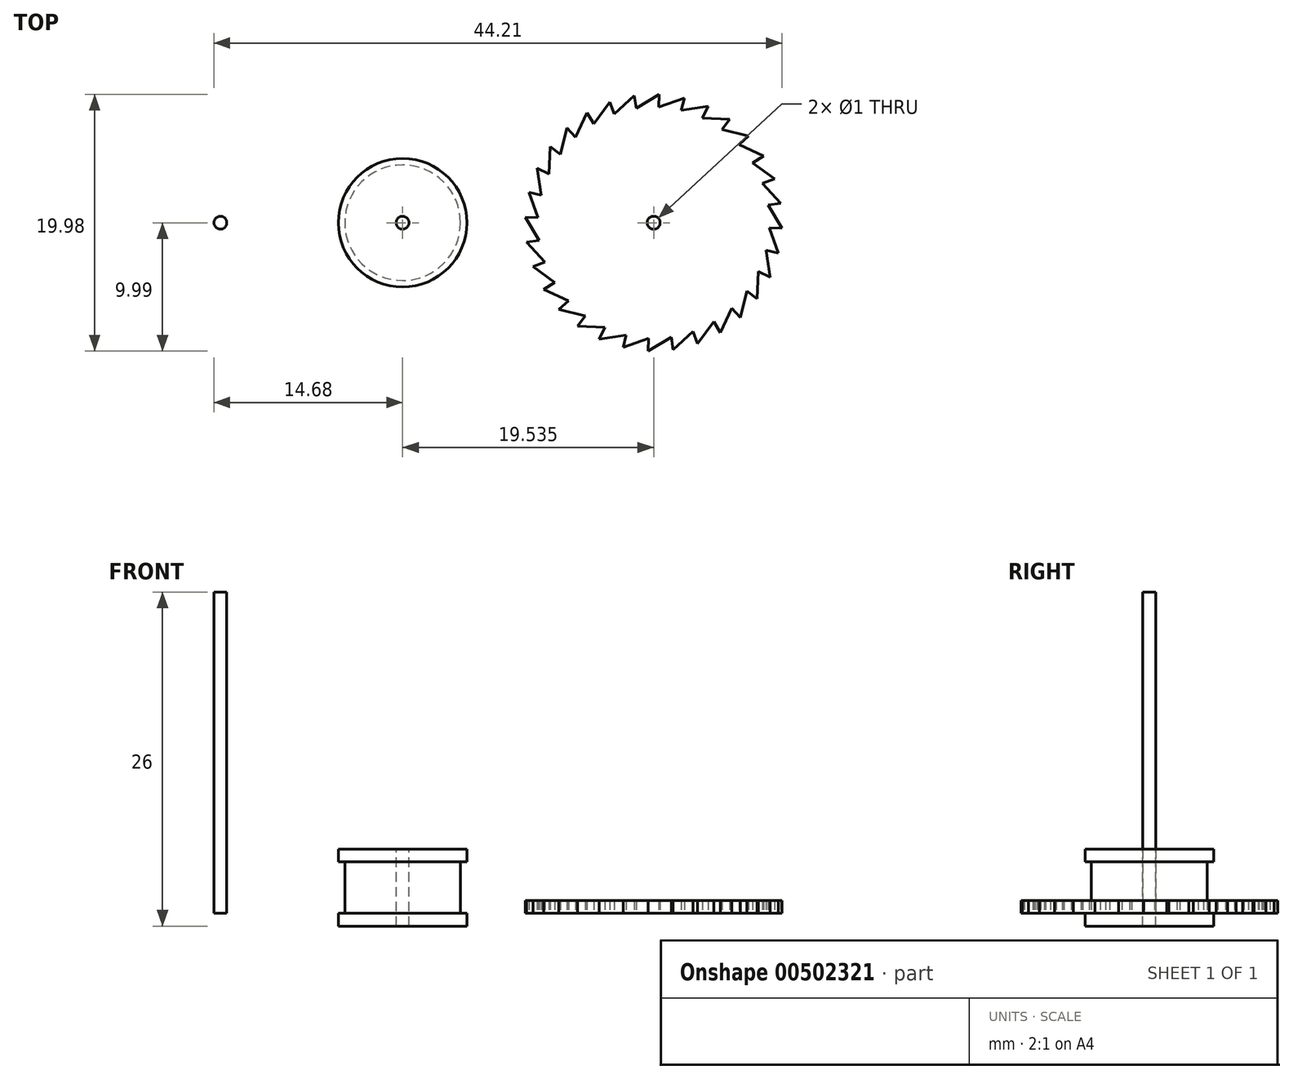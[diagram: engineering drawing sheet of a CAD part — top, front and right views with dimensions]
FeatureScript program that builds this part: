
annotation { "Feature Type Name" : "Feature", "Feature Type Description" : "" }
export const myFeature = defineFeature(function(context is Context, id is Id, definition is map)
    precondition{}
    {
        {
            var Q0;
            Q0=qCreatedBy(makeId("Top.planeOp"),FACE);
            var sketch = newSketch(context, id + "F0", { "sketchPlane" : qUnion([Q0])});
            skCircle(sketch, "E0", {"center": v(0, 0) * mm, "radius": 5 * mm});
            skCircle(sketch, "E1", {"center": v(0, 0) * mm, "radius": 4.5 * mm});
            skCircle(sketch, "E2", {"center": v(0, 0) * mm, "radius": 0.5 * mm});
            skSolve(sketch);
        }
        {
            var Q0;
            Q0=makeQuery(id+"F0.imprint","IMPRINT",FACE,{"disambiguationData":[TD([[makeQuery(id+"F0.imprint","IMPRINT",EDGE,{"derivedFrom":sQuery(id+"F0.wireOp",EDGE,"E0")}),1.0]])]});
            var Q1;
            Q1=makeQuery(id+"F0.imprint","IMPRINT",FACE,{"disambiguationData":[TD([[makeQuery(id+"F0.imprint","IMPRINT",EDGE,{"derivedFrom":sQuery(id+"F0.wireOp",EDGE,"E1")}),1.0]])]});
            extrude(context, id + "F1", {"entities" : qUnion([Q0, Q1]), "oppositeDirection" : true, "depth" : 1 * mm, "offsetDistance" : 25 * mm});
        }
        {
            var Q0;
            Q0=makeQuery(id+"F0.imprint","IMPRINT",FACE,{"disambiguationData":[TD([[makeQuery(id+"F0.imprint","IMPRINT",EDGE,{"derivedFrom":sQuery(id+"F0.wireOp",EDGE,"E1")}),1.0]])]});
            extrude(context, id + "F2", {"entities" : qUnion([Q0]), "operationType" : NewBodyOperationType.ADD, "depth" : 2 * mm, "offsetDistance" : 25 * mm});
        }
        {
            var Q0;
            Q0=makeQuery(id+"F1.opExtrude","SWEPT_BODY",BODY,{"disambiguationData":[OSD([sQuery(id+"F0.wireOp",EDGE,"E0")])]});
            var Q1;
            Q1=makeQuery(id+"F2.opExtrude","CAP_FACE",FACE,{"disambiguationData":[OSD([sQuery(id+"F0.wireOp",EDGE,"E1")])],"isStart":false});
            mirror(context, id + "F3", {"operationType" : NewBodyOperationType.ADD, "entities" : qUnion([Q0]), "mirrorPlane" : qUnion([Q1])});
        }
        {
            var Q0;
            Q0=qCreatedBy(makeId("Top.planeOp"),FACE);
            var sketch = newSketch(context, id + "F4", { "sketchPlane" : qUnion([Q0])});
            skCircle(sketch, "E3", {"center": v(-14.18, 0) * mm, "radius": 0.5 * mm});
            skCircle(sketch, "E4", {"center": v(19.53, 0) * mm, "radius": 9 * mm, "construction": true});
            skCircle(sketch, "E5", {"center": v(19.53, 0) * mm, "radius": 0.5 * mm});
            skCircle(sketch, "E6", {"center": v(19.53, 0) * mm, "radius": 10 * mm, "construction": true});
            skLineSegment(sketch, "E7", {"start": v(19.53, 0) * mm, "end": v(21.91, 9.71) * mm, "construction": true});
            skLineSegment(sketch, "E8.1.0", {"start": v(19.53, 0) * mm, "end": v(19.97, 10) * mm, "construction": true});
            skLineSegment(sketch, "E8.2.0", {"start": v(19.53, 0) * mm, "end": v(18.02, 9.88) * mm, "construction": true});
            skLineSegment(sketch, "E8.3.0", {"start": v(19.53, 0) * mm, "end": v(16.12, 9.4) * mm, "construction": true});
            skLineSegment(sketch, "E8.4.0", {"start": v(19.53, 0) * mm, "end": v(14.35, 8.55) * mm, "construction": true});
            skLineSegment(sketch, "E8.5.0", {"start": v(19.53, 0) * mm, "end": v(12.78, 7.37) * mm, "construction": true});
            skLineSegment(sketch, "E8.6.0", {"start": v(19.53, 0) * mm, "end": v(11.47, 5.92) * mm, "construction": true});
            skLineSegment(sketch, "E8.7.0", {"start": v(19.53, 0) * mm, "end": v(10.47, 4.23) * mm, "construction": true});
            skLineSegment(sketch, "E8.8.0", {"start": v(19.53, 0) * mm, "end": v(9.82, 2.38) * mm, "construction": true});
            skLineSegment(sketch, "E8.9.0", {"start": v(19.53, 0) * mm, "end": v(9.54, 0.44) * mm, "construction": true});
            skLineSegment(sketch, "E8.10.0", {"start": v(19.53, 0) * mm, "end": v(9.65, -1.52) * mm, "construction": true});
            skLineSegment(sketch, "E8.11.0", {"start": v(19.53, 0) * mm, "end": v(10.14, -3.42) * mm, "construction": true});
            skLineSegment(sketch, "E8.12.0", {"start": v(19.53, 0) * mm, "end": v(10.98, -5.18) * mm, "construction": true});
            skLineSegment(sketch, "E8.13.0", {"start": v(19.53, 0) * mm, "end": v(12.16, -6.75) * mm, "construction": true});
            skLineSegment(sketch, "E8.14.0", {"start": v(19.53, 0) * mm, "end": v(13.62, -8.06) * mm, "construction": true});
            skLineSegment(sketch, "E8.15.0", {"start": v(19.53, 0) * mm, "end": v(15.3, -9.06) * mm, "construction": true});
            skLineSegment(sketch, "E8.16.0", {"start": v(19.53, 0) * mm, "end": v(17.15, -9.71) * mm, "construction": true});
            skLineSegment(sketch, "E8.17.0", {"start": v(19.53, 0) * mm, "end": v(19.1, -10) * mm, "construction": true});
            skLineSegment(sketch, "E8.18.0", {"start": v(19.53, 0) * mm, "end": v(21.05, -9.88) * mm, "construction": true});
            skLineSegment(sketch, "E8.19.0", {"start": v(19.53, 0) * mm, "end": v(22.95, -9.4) * mm, "construction": true});
            skLineSegment(sketch, "E8.20.0", {"start": v(19.53, 0) * mm, "end": v(24.72, -8.55) * mm, "construction": true});
            skLineSegment(sketch, "E8.21.0", {"start": v(19.53, 0) * mm, "end": v(26.29, -7.37) * mm, "construction": true});
            skLineSegment(sketch, "E8.22.0", {"start": v(19.53, 0) * mm, "end": v(27.6, -5.92) * mm, "construction": true});
            skLineSegment(sketch, "E8.23.0", {"start": v(19.53, 0) * mm, "end": v(28.6, -4.23) * mm, "construction": true});
            skLineSegment(sketch, "E8.24.0", {"start": v(19.53, 0) * mm, "end": v(29.25, -2.38) * mm, "construction": true});
            skLineSegment(sketch, "E8.25.0", {"start": v(19.53, 0) * mm, "end": v(29.53, -0.44) * mm, "construction": true});
            skLineSegment(sketch, "E8.26.0", {"start": v(19.53, 0) * mm, "end": v(29.42, 1.52) * mm, "construction": true});
            skLineSegment(sketch, "E8.27.0", {"start": v(19.53, 0) * mm, "end": v(28.93, 3.42) * mm, "construction": true});
            skLineSegment(sketch, "E8.28.0", {"start": v(19.53, 0) * mm, "end": v(28.09, 5.18) * mm, "construction": true});
            skLineSegment(sketch, "E8.29.0", {"start": v(19.53, 0) * mm, "end": v(26.9, 6.75) * mm, "construction": true});
            skLineSegment(sketch, "E8.30.0", {"start": v(19.53, 0) * mm, "end": v(25.45, 8.06) * mm, "construction": true});
            skLineSegment(sketch, "E8.31.0", {"start": v(19.53, 0) * mm, "end": v(23.76, 9.06) * mm, "construction": true});
            skLineSegment(sketch, "E9", {"start": v(21.68, 8.74) * mm, "end": v(21.91, 9.71) * mm});
            skLineSegment(sketch, "E10", {"start": v(21.91, 9.71) * mm, "end": v(19.93, 9) * mm});
            skLineSegment(sketch, "E11.1.0", {"start": v(19.97, 10) * mm, "end": v(18.17, 8.9) * mm});
            skLineSegment(sketch, "E11.1.1", {"start": v(19.93, 9) * mm, "end": v(19.97, 10) * mm});
            skLineSegment(sketch, "E11.2.0", {"start": v(18.02, 9.88) * mm, "end": v(16.46, 8.46) * mm});
            skLineSegment(sketch, "E11.2.1", {"start": v(18.17, 8.9) * mm, "end": v(18.02, 9.88) * mm});
            skLineSegment(sketch, "E11.3.0", {"start": v(16.12, 9.4) * mm, "end": v(14.87, 7.7) * mm});
            skLineSegment(sketch, "E11.3.1", {"start": v(16.46, 8.46) * mm, "end": v(16.12, 9.4) * mm});
            skLineSegment(sketch, "E11.4.0", {"start": v(14.35, 8.55) * mm, "end": v(13.46, 6.64) * mm});
            skLineSegment(sketch, "E11.4.1", {"start": v(14.87, 7.7) * mm, "end": v(14.35, 8.55) * mm});
            skLineSegment(sketch, "E11.5.0", {"start": v(12.78, 7.37) * mm, "end": v(12.28, 5.32) * mm});
            skLineSegment(sketch, "E11.5.1", {"start": v(13.46, 6.64) * mm, "end": v(12.78, 7.37) * mm});
            skLineSegment(sketch, "E11.6.0", {"start": v(11.47, 5.92) * mm, "end": v(11.38, 3.8) * mm});
            skLineSegment(sketch, "E11.6.1", {"start": v(12.28, 5.32) * mm, "end": v(11.47, 5.92) * mm});
            skLineSegment(sketch, "E11.7.0", {"start": v(10.47, 4.23) * mm, "end": v(10.8, 2.14) * mm});
            skLineSegment(sketch, "E11.7.1", {"start": v(11.38, 3.8) * mm, "end": v(10.47, 4.23) * mm});
            skLineSegment(sketch, "E11.8.0", {"start": v(9.82, 2.38) * mm, "end": v(10.54, 0.4) * mm});
            skLineSegment(sketch, "E11.8.1", {"start": v(10.8, 2.14) * mm, "end": v(9.82, 2.38) * mm});
            skLineSegment(sketch, "E11.9.0", {"start": v(9.54, 0.44) * mm, "end": v(10.64, -1.37) * mm});
            skLineSegment(sketch, "E11.9.1", {"start": v(10.54, 0.4) * mm, "end": v(9.54, 0.44) * mm});
            skLineSegment(sketch, "E11.10.0", {"start": v(9.65, -1.52) * mm, "end": v(11.08, -3.08) * mm});
            skLineSegment(sketch, "E11.10.1", {"start": v(10.64, -1.37) * mm, "end": v(9.65, -1.52) * mm});
            skLineSegment(sketch, "E11.11.0", {"start": v(10.14, -3.42) * mm, "end": v(11.84, -4.67) * mm});
            skLineSegment(sketch, "E11.11.1", {"start": v(11.08, -3.08) * mm, "end": v(10.14, -3.42) * mm});
            skLineSegment(sketch, "E11.12.0", {"start": v(10.98, -5.18) * mm, "end": v(12.9, -6.08) * mm});
            skLineSegment(sketch, "E11.12.1", {"start": v(11.84, -4.67) * mm, "end": v(10.98, -5.18) * mm});
            skLineSegment(sketch, "E11.13.0", {"start": v(12.16, -6.75) * mm, "end": v(14.21, -7.26) * mm});
            skLineSegment(sketch, "E11.13.1", {"start": v(12.9, -6.08) * mm, "end": v(12.16, -6.75) * mm});
            skLineSegment(sketch, "E11.14.0", {"start": v(13.62, -8.06) * mm, "end": v(15.73, -8.16) * mm});
            skLineSegment(sketch, "E11.14.1", {"start": v(14.21, -7.26) * mm, "end": v(13.62, -8.06) * mm});
            skLineSegment(sketch, "E11.15.0", {"start": v(15.3, -9.06) * mm, "end": v(17.4, -8.74) * mm});
            skLineSegment(sketch, "E11.15.1", {"start": v(15.73, -8.16) * mm, "end": v(15.3, -9.06) * mm});
            skLineSegment(sketch, "E11.16.0", {"start": v(17.15, -9.71) * mm, "end": v(19.14, -9) * mm});
            skLineSegment(sketch, "E11.16.1", {"start": v(17.4, -8.74) * mm, "end": v(17.15, -9.71) * mm});
            skLineSegment(sketch, "E11.17.0", {"start": v(19.1, -10) * mm, "end": v(20.9, -8.9) * mm});
            skLineSegment(sketch, "E11.17.1", {"start": v(19.14, -9) * mm, "end": v(19.1, -10) * mm});
            skLineSegment(sketch, "E11.18.0", {"start": v(21.05, -9.88) * mm, "end": v(22.61, -8.46) * mm});
            skLineSegment(sketch, "E11.18.1", {"start": v(20.9, -8.9) * mm, "end": v(21.05, -9.88) * mm});
            skLineSegment(sketch, "E11.19.0", {"start": v(22.95, -9.4) * mm, "end": v(24.2, -7.7) * mm});
            skLineSegment(sketch, "E11.19.1", {"start": v(22.61, -8.46) * mm, "end": v(22.95, -9.4) * mm});
            skLineSegment(sketch, "E11.20.0", {"start": v(24.72, -8.55) * mm, "end": v(25.61, -6.64) * mm});
            skLineSegment(sketch, "E11.20.1", {"start": v(24.2, -7.7) * mm, "end": v(24.72, -8.55) * mm});
            skLineSegment(sketch, "E11.21.0", {"start": v(26.29, -7.37) * mm, "end": v(26.8, -5.32) * mm});
            skLineSegment(sketch, "E11.21.1", {"start": v(25.61, -6.64) * mm, "end": v(26.29, -7.37) * mm});
            skLineSegment(sketch, "E11.22.0", {"start": v(27.6, -5.92) * mm, "end": v(27.7, -3.8) * mm});
            skLineSegment(sketch, "E11.22.1", {"start": v(26.8, -5.32) * mm, "end": v(27.6, -5.92) * mm});
            skLineSegment(sketch, "E11.23.0", {"start": v(28.6, -4.23) * mm, "end": v(28.28, -2.14) * mm});
            skLineSegment(sketch, "E11.23.1", {"start": v(27.7, -3.8) * mm, "end": v(28.6, -4.23) * mm});
            skLineSegment(sketch, "E11.24.0", {"start": v(29.25, -2.38) * mm, "end": v(28.53, -0.4) * mm});
            skLineSegment(sketch, "E11.24.1", {"start": v(28.28, -2.14) * mm, "end": v(29.25, -2.38) * mm});
            skLineSegment(sketch, "E11.25.0", {"start": v(29.53, -0.44) * mm, "end": v(28.43, 1.37) * mm});
            skLineSegment(sketch, "E11.25.1", {"start": v(28.53, -0.4) * mm, "end": v(29.53, -0.44) * mm});
            skLineSegment(sketch, "E11.26.0", {"start": v(29.42, 1.52) * mm, "end": v(28, 3.08) * mm});
            skLineSegment(sketch, "E11.26.1", {"start": v(28.43, 1.37) * mm, "end": v(29.42, 1.52) * mm});
            skLineSegment(sketch, "E11.27.0", {"start": v(28.93, 3.42) * mm, "end": v(27.23, 4.67) * mm});
            skLineSegment(sketch, "E11.27.1", {"start": v(28, 3.08) * mm, "end": v(28.93, 3.42) * mm});
            skLineSegment(sketch, "E11.28.0", {"start": v(28.09, 5.18) * mm, "end": v(26.17, 6.08) * mm});
            skLineSegment(sketch, "E11.28.1", {"start": v(27.23, 4.67) * mm, "end": v(28.09, 5.18) * mm});
            skLineSegment(sketch, "E11.29.0", {"start": v(26.9, 6.75) * mm, "end": v(24.86, 7.26) * mm});
            skLineSegment(sketch, "E11.29.1", {"start": v(26.17, 6.08) * mm, "end": v(26.9, 6.75) * mm});
            skLineSegment(sketch, "E11.30.0", {"start": v(25.45, 8.06) * mm, "end": v(23.34, 8.16) * mm});
            skLineSegment(sketch, "E11.30.1", {"start": v(24.86, 7.26) * mm, "end": v(25.45, 8.06) * mm});
            skLineSegment(sketch, "E11.31.0", {"start": v(23.76, 9.06) * mm, "end": v(21.68, 8.74) * mm});
            skLineSegment(sketch, "E11.31.1", {"start": v(23.34, 8.16) * mm, "end": v(23.76, 9.06) * mm});
            skSolve(sketch);
        }
        {
            var Q0;
            Q0=makeQuery(id+"F4.imprint","IMPRINT",FACE,{"disambiguationData":[TD([[makeQuery(id+"F4.imprint","IMPRINT",EDGE,{"derivedFrom":sQuery(id+"F4.wireOp",EDGE,"E5")}),-1.0]])]});
            extrude(context, id + "F5", {"entities" : qUnion([Q0]), "depth" : 1 * mm, "offsetDistance" : 25 * mm});
        }
        {
            var Q0;
            Q0=makeQuery(id+"F4.imprint","IMPRINT",FACE,{"disambiguationData":[TD([[makeQuery(id+"F4.imprint","IMPRINT",EDGE,{"derivedFrom":sQuery(id+"F4.wireOp",EDGE,"E3")}),1.0]])]});
            extrude(context, id + "F6", {"entities" : qUnion([Q0]), "depth" : 25 * mm, "offsetDistance" : 25 * mm});
        }
    });
